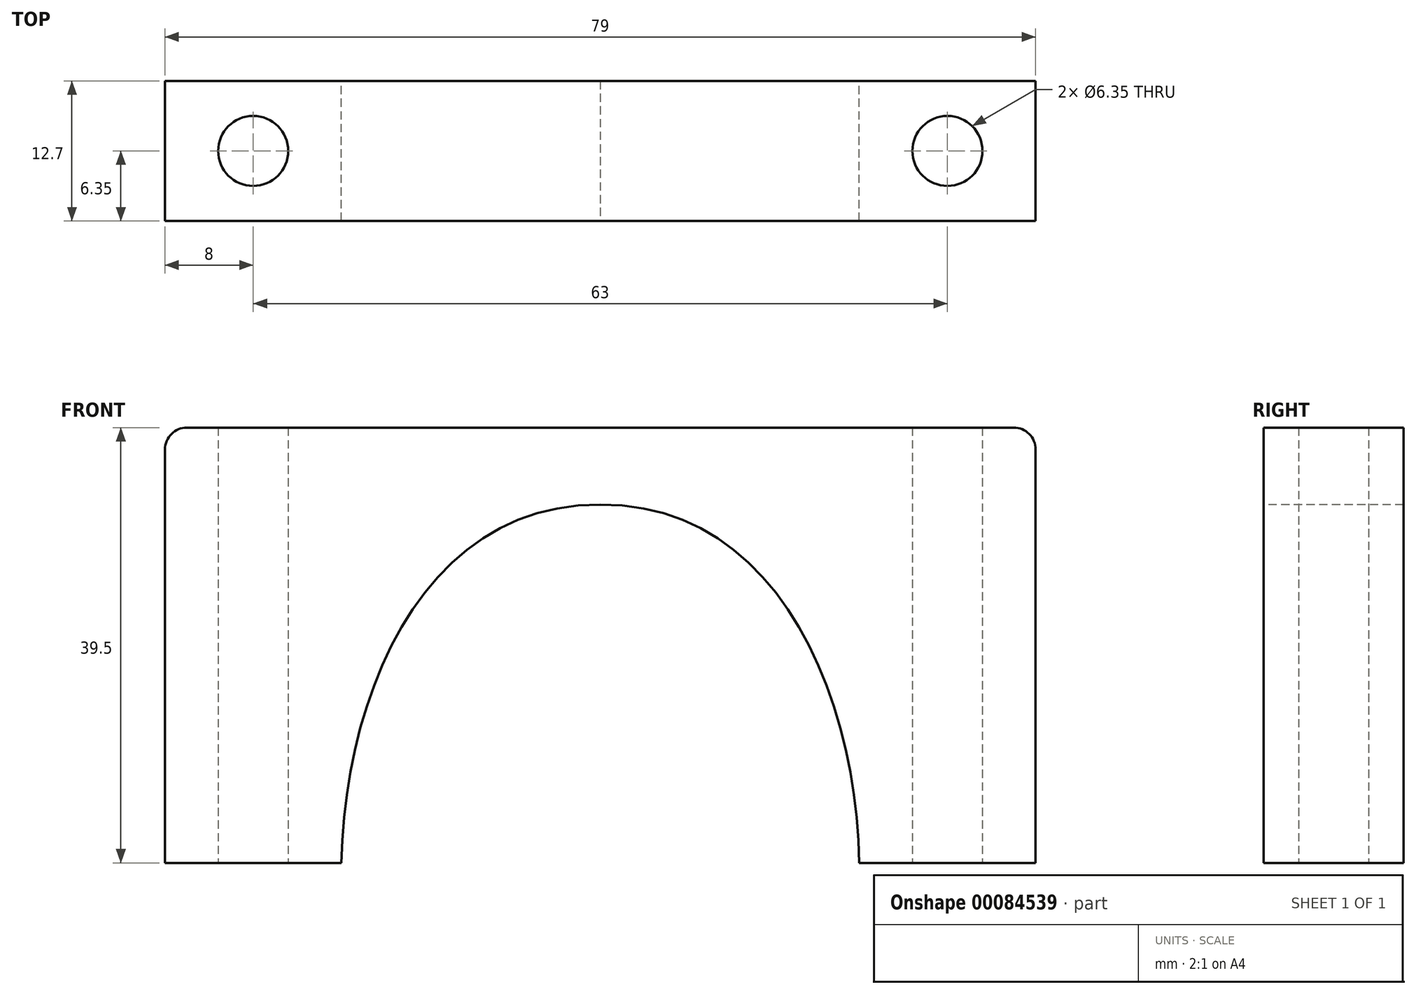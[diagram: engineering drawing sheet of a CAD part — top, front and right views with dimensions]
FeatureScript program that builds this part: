
annotation { "Feature Type Name" : "Feature", "Feature Type Description" : "" }
export const myFeature = defineFeature(function(context is Context, id is Id, definition is map)
    precondition{}
    {
        {
            var Q0;
            Q0=qCreatedBy(makeId("Front.planeOp"),FACE);
            var sketch = newSketch(context, id + "F0", { "sketchPlane" : qUnion([Q0]) });
            skPoint(sketch, "E0", {"position": v(0.8, 9.7) * mm});
            skPoint(sketch, "E1", {"position": v(2.4, 15.7) * mm});
            skPoint(sketch, "E2", {"position": v(6.6, 23.8) * mm});
            skPoint(sketch, "E3", {"position": v(12.9, 30.8) * mm});
            skPoint(sketch, "E4", {"position": v(19, 33.2) * mm});
            skPoint(sketch, "E5", {"position": v(23.5, 33.5) * mm});
            skLineSegment(sketch, "E6", {"start": v(23.5, 33.5) * mm, "end": v(23.5, 0) * mm, "construction": true});
            skPoint(sketch, "E7", {"position": v(3.4, 18.7) * mm});
            skPoint(sketch, "E8", {"position": v(9.6, 28) * mm});
            skFitSpline(sketch, "E9", {"points": [v(0, 0) * mm, v(23.5, 33.5) * mm], "startDerivative": vector(0, 48.1) * mm, "endDerivative": vector(48.2, -0.45) * mm});
            skFitSpline(sketch, "E10.MirrorCS", {"points": [v(47, 0) * mm, v(23.5, 33.5) * mm], "startDerivative": vector(0, 48.1) * mm, "endDerivative": vector(-48.2, -0.45) * mm});
            skFitSpline(sketch, "E11.0", {"points": [v(53, 0) * mm, v(53, 2.24) * mm, v(52.74, 6.75) * mm, v(51.56, 13.47) * mm, v(49.53, 19.97) * mm, v(46.58, 26.03) * mm, v(43.25, 30.55) * mm, v(39.98, 33.67) * mm, v(37.22, 35.7) * mm, v(34.16, 37.38) * mm, v(30.81, 38.61) * mm, v(27.23, 39.36) * mm, v(24.72, 39.51) * mm, v(23.44, 39.5) * mm]});
            skFitSpline(sketch, "E11.1", {"points": [v(-6, 0) * mm, v(-6, 2.24) * mm, v(-5.74, 6.75) * mm, v(-4.56, 13.47) * mm, v(-2.53, 19.97) * mm, v(0.42, 26.03) * mm, v(3.75, 30.55) * mm, v(7.02, 33.67) * mm, v(9.78, 35.7) * mm, v(12.84, 37.38) * mm, v(16.19, 38.61) * mm, v(19.77, 39.36) * mm, v(22.28, 39.51) * mm, v(23.56, 39.5) * mm]});
            skLineSegment(sketch, "E12", {"start": v(0, 0) * mm, "end": v(-6, 0) * mm});
            skLineSegment(sketch, "E13.MirrorCS", {"start": v(47, 0) * mm, "end": v(53, 0) * mm});
            skLineSegment(sketch, "E14", {"start": v(-5.13, 10) * mm, "end": v(-16, 10) * mm});
            skLineSegment(sketch, "E15", {"start": v(-6, 0) * mm, "end": v(-16, 0) * mm});
            skLineSegment(sketch, "E16", {"start": v(-16, 0) * mm, "end": v(-16, 10) * mm});
            skLineSegment(sketch, "E17.MirrorCS", {"start": v(52.13, 10) * mm, "end": v(63, 10) * mm});
            skLineSegment(sketch, "E18.MirrorCS", {"start": v(63, 0) * mm, "end": v(63, 10) * mm});
            skLineSegment(sketch, "E19.MirrorCS", {"start": v(53, 0) * mm, "end": v(63, 0) * mm});
            skLineSegment(sketch, "E20", {"start": v(-16, 10) * mm, "end": v(-16, 39.5) * mm});
            skLineSegment(sketch, "E21", {"start": v(-16, 39.5) * mm, "end": v(23.5, 39.5) * mm});
            skLineSegment(sketch, "E22.MirrorCS", {"start": v(63, 10) * mm, "end": v(63, 39.5) * mm});
            skLineSegment(sketch, "E23.MirrorCS", {"start": v(63, 39.5) * mm, "end": v(23.5, 39.5) * mm});
            skSolve(sketch);
        }
        {
            var Q0;
            Q0 = qSketchRegion(id + "F0", true);
            extrude(context, id + "F1", {"entities" : qUnion([Q0]), "depth" : 12.7 * mm});
        }
        {
            var Q0;
            Q0=makeQuery(id+"F1.opExtrude","CAP_FACE",FACE,{"disambiguationData":[OSD([sQuery(id+"F0.wireOp",EDGE,"E9"),sQuery(id+"F0.wireOp",EDGE,"E10.MirrorCS"),sQuery(id+"F0.wireOp",EDGE,"E11.0"),sQuery(id+"F0.wireOp",EDGE,"E11.1"),sQuery(id+"F0.wireOp",EDGE,"E12"),sQuery(id+"F0.wireOp",EDGE,"E13.MirrorCS"),sQuery(id+"F0.wireOp",EDGE,"E15"),sQuery(id+"F0.wireOp",EDGE,"E16"),sQuery(id+"F0.wireOp",EDGE,"E18.MirrorCS"),sQuery(id+"F0.wireOp",EDGE,"E19.MirrorCS"),sQuery(id+"F0.wireOp",EDGE,"E20"),sQuery(id+"F0.wireOp",EDGE,"E21"),sQuery(id+"F0.wireOp",EDGE,"E22.MirrorCS"),sQuery(id+"F0.wireOp",EDGE,"E23.MirrorCS")])],"isStart":false});
            var sketch = newSketch(context, id + "F2", { "sketchPlane" : qUnion([Q0]) });
            skLineSegment(sketch, "E24", {"start": v(-16, 39.5) * mm, "end": v(-16, 40.5) * mm});
            skLineSegment(sketch, "E25", {"start": v(-16, 40.5) * mm, "end": v(63, 40.5) * mm});
            skLineSegment(sketch, "E26", {"start": v(63, 40.5) * mm, "end": v(63, 39.5) * mm});
            skLineSegment(sketch, "E27", {"start": v(63, 39.5) * mm, "end": v(-16, 39.5) * mm});
            skSolve(sketch);
        }
        {
            var Q0;
            Q0 = qSketchRegion(id + "F2", true);
            extrude(context, id + "F3", {"entities" : qUnion([Q0]), "operationType" : NewBodyOperationType.ADD, "oppositeDirection" : true, "depth" : 12.7 * mm});
        }
        {
            var Q0;
            Q0=makeQuery(id+"F1.opExtrude","SWEPT_FACE",FACE,{"disambiguationData":[OSD([sQuery(id+"F0.wireOp",EDGE,"E12"),sQuery(id+"F0.wireOp",EDGE,"E15")])]});
            var sketch = newSketch(context, id + "F4", { "sketchPlane" : qUnion([Q0]) });
            skCircle(sketch, "E28", {"center": v(-8, 6.35) * mm, "radius": 3.18 * mm});
            skPoint(sketch, "E28.centerSnap0", {"position": v(-16, 6.35) * mm});
            skFitSpline(sketch, "E29.0", {"points": [v(23.5, 19.05) * mm, v(23.5, 12.7) * mm, v(23.5, 6.35) * mm, v(23.5, 0) * mm], "construction": true});
            skSolve(sketch);
        }
        {
            var Q0;
            Q0 = qSketchRegion(id + "F4", true);
            extrude(context, id + "F5", {"entities" : qUnion([Q0]), "operationType" : NewBodyOperationType.REMOVE, "endBound" : BoundingType.THROUGH_ALL, "oppositeDirection" : true, "depth" : 25 * mm});
        }
        {
            var Q0;
            Q0=makeQuery(id+"F1.opExtrude","SWEPT_FACE",FACE,{"disambiguationData":[OSD([sQuery(id+"F0.wireOp",EDGE,"E13.MirrorCS"),sQuery(id+"F0.wireOp",EDGE,"E19.MirrorCS")])]});
            var sketch = newSketch(context, id + "F6", { "sketchPlane" : qUnion([Q0]) });
            skCircle(sketch, "E30", {"center": v(55, 6.35) * mm, "radius": 3.18 * mm});
            skPoint(sketch, "E30.centerSnap0", {"position": v(63, 6.35) * mm});
            skSolve(sketch);
        }
        {
            var Q0;
            Q0 = qSketchRegion(id + "F6", true);
            extrude(context, id + "F7", {"entities" : qUnion([Q0]), "operationType" : NewBodyOperationType.REMOVE, "endBound" : BoundingType.UP_TO_NEXT, "oppositeDirection" : true, "depth" : 25 * mm});
        }
        {
            var Q0;
            Q0=qCreatedBy(makeId("Front.planeOp"),FACE);
            var sketch = newSketch(context, id + "F8", { "sketchPlane" : qUnion([Q0]) });
            skLineSegment(sketch, "E31.bottom", {"start": v(-18.85, 1) * mm, "end": v(65.58, 1) * mm});
            skLineSegment(sketch, "E31.top", {"start": v(-18.85, -2.48) * mm, "end": v(65.58, -2.48) * mm});
            skLineSegment(sketch, "E31.left", {"start": v(-18.85, 1) * mm, "end": v(-18.85, -2.48) * mm});
            skLineSegment(sketch, "E31.right", {"start": v(65.58, 1) * mm, "end": v(65.58, -2.48) * mm});
            skSolve(sketch);
        }
        {
            var Q0;
            Q0 = qSketchRegion(id + "F8", true);
            extrude(context, id + "F9", {"entities" : qUnion([Q0]), "operationType" : NewBodyOperationType.REMOVE, "depth" : 25 * mm});
        }
        {
            var Q0;
            Q0=makeQuery(id+"F3.opExtrude","SWEPT_EDGE",EDGE,{"disambiguationData":[OSD([sQuery(id+"F2.wireOp",EDGE,"E24"),sQuery(id+"F2.wireOp",EDGE,"E25")])]});
            var Q1;
            Q1=makeQuery(id+"F3.opExtrude","SWEPT_EDGE",EDGE,{"disambiguationData":[OSD([sQuery(id+"F2.wireOp",EDGE,"E25"),sQuery(id+"F2.wireOp",EDGE,"E26")])]});
            fillet(context, id + "F10", {"entities" : qUnion([Q0, Q1]), "radius" : 2 * mm, "tangentPropagation" : true, "conicFillet" : false});
        }
    });
